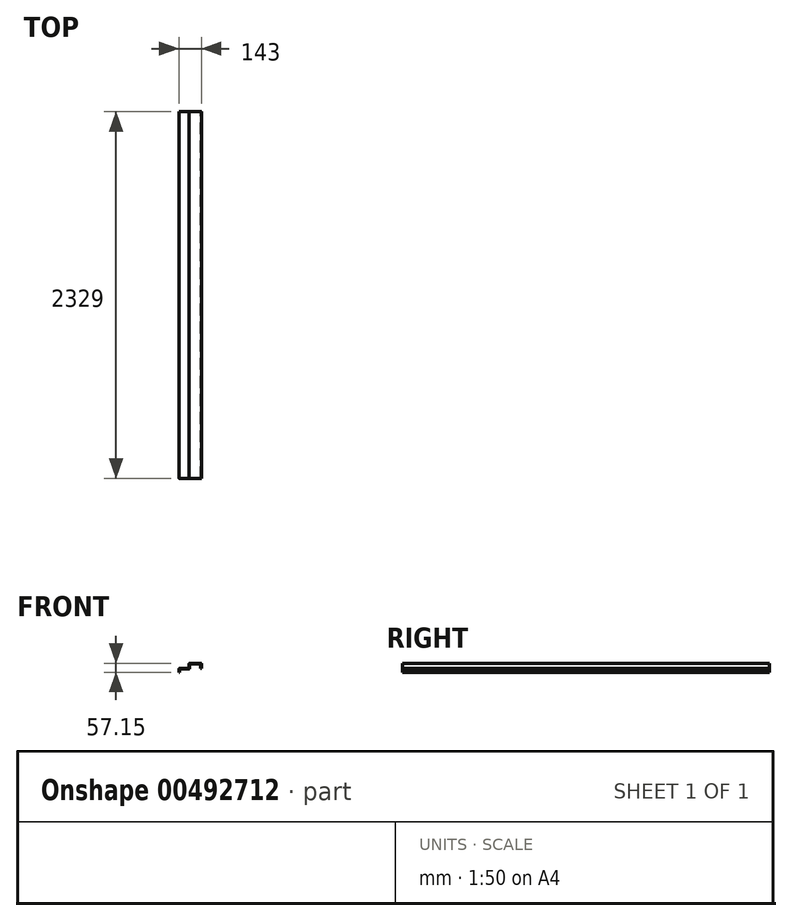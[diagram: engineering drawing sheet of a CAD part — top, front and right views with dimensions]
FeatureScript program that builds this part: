
annotation { "Feature Type Name" : "Feature", "Feature Type Description" : "" }
export const myFeature = defineFeature(function(context is Context, id is Id, definition is map)
    precondition{}
    {
        {
            var Q0;
            Q0=qCreatedBy(makeId("Front.planeOp"),FACE);
            var sketch = newSketch(context, id + "F0", { "sketchPlane" : qUnion([Q0])});
            skLineSegment(sketch, "E0", {"start": v(10, 0) * mm, "end": v(142, 0) * mm});
            skLineSegment(sketch, "E1", {"start": v(0, 10) * mm, "end": v(0, 120) * mm});
            skLineSegment(sketch, "E2", {"start": v(152, 10) * mm, "end": v(152, 147.25) * mm});
            skLineSegment(sketch, "E3.1", {"start": v(14.5, 4.5) * mm, "end": v(137.5, 4.5) * mm});
            skLineSegment(sketch, "E4", {"start": v(0, 120) * mm, "end": v(4.5, 120) * mm});
            skLineSegment(sketch, "E5", {"start": v(147.5, 147.25) * mm, "end": v(152, 147.25) * mm});
            skPoint(sketch, "E6.visualSharp", {"position": v(152, 0) * mm});
            skArc(sketch, "E6.filletArc", {"start": v(142, 0) * mm, "mid": v(149.07, 2.93) * mm, "end": v(152, 10) * mm});
            skPoint(sketch, "E7.visualSharp", {"position": v(147.5, 4.5) * mm});
            skArc(sketch, "E7.filletArc", {"start": v(137.5, 4.5) * mm, "mid": v(144.57, 7.43) * mm, "end": v(147.5, 14.5) * mm});
            skPoint(sketch, "E8.visualSharp", {"position": v(0, 0) * mm});
            skArc(sketch, "E8.filletArc", {"start": v(0, 10) * mm, "mid": v(2.93, 2.93) * mm, "end": v(10, 0) * mm});
            skPoint(sketch, "E9.visualSharp", {"position": v(4.5, 4.5) * mm});
            skArc(sketch, "E9.filletArc", {"start": v(4.5, 14.5) * mm, "mid": v(7.43, 7.43) * mm, "end": v(14.5, 4.5) * mm});
            skLineSegment(sketch, "E10", {"start": v(147.5, 146.75) * mm, "end": v(147.5, 120) * mm});
            skLineSegment(sketch, "E11", {"start": v(4.5, 94.6) * mm, "end": v(4.5, 115) * mm});
            skLineSegment(sketch, "E12", {"start": v(9.5, 120) * mm, "end": v(63, 120) * mm});
            skLineSegment(sketch, "E13", {"start": v(68, 125) * mm, "end": v(68, 146.75) * mm});
            skLineSegment(sketch, "E14", {"start": v(73, 151.75) * mm, "end": v(142.5, 151.75) * mm});
            skLineSegment(sketch, "E15.0", {"start": v(143, 142.25) * mm, "end": v(143, 120) * mm});
            skLineSegment(sketch, "E15.1", {"start": v(9, 94.6) * mm, "end": v(9, 110.5) * mm});
            skLineSegment(sketch, "E15.2", {"start": v(14, 115.5) * mm, "end": v(67.5, 115.5) * mm});
            skLineSegment(sketch, "E15.3", {"start": v(72.5, 120.5) * mm, "end": v(72.5, 142.25) * mm});
            skLineSegment(sketch, "E15.4", {"start": v(77.5, 147.25) * mm, "end": v(138, 147.25) * mm});
            skPoint(sketch, "E16.visualSharp", {"position": v(147.5, 151.75) * mm});
            skArc(sketch, "E16.filletArc", {"start": v(147.5, 146.75) * mm, "mid": v(146.04, 150.29) * mm, "end": v(142.5, 151.75) * mm});
            skPoint(sketch, "E17.visualSharp", {"position": v(143, 147.25) * mm});
            skArc(sketch, "E17.filletArc", {"start": v(143, 142.25) * mm, "mid": v(141.54, 145.79) * mm, "end": v(138, 147.25) * mm});
            skPoint(sketch, "E18.visualSharp", {"position": v(72.5, 147.25) * mm});
            skArc(sketch, "E18.filletArc", {"start": v(77.5, 147.25) * mm, "mid": v(73.96, 145.79) * mm, "end": v(72.5, 142.25) * mm});
            skPoint(sketch, "E19.visualSharp", {"position": v(68, 151.75) * mm});
            skArc(sketch, "E19.filletArc", {"start": v(73, 151.75) * mm, "mid": v(69.46, 150.29) * mm, "end": v(68, 146.75) * mm});
            skPoint(sketch, "E20.visualSharp", {"position": v(72.5, 115.5) * mm});
            skArc(sketch, "E20.filletArc", {"start": v(67.5, 115.5) * mm, "mid": v(71.04, 116.96) * mm, "end": v(72.5, 120.5) * mm});
            skPoint(sketch, "E21.visualSharp", {"position": v(68, 120) * mm});
            skArc(sketch, "E21.filletArc", {"start": v(63, 120) * mm, "mid": v(66.54, 121.46) * mm, "end": v(68, 125) * mm});
            skPoint(sketch, "E22.visualSharp", {"position": v(9, 115.5) * mm});
            skArc(sketch, "E22.filletArc", {"start": v(14, 115.5) * mm, "mid": v(10.46, 114.04) * mm, "end": v(9, 110.5) * mm});
            skPoint(sketch, "E23.visualSharp", {"position": v(4.5, 120) * mm});
            skArc(sketch, "E23.filletArc", {"start": v(9.5, 120) * mm, "mid": v(5.96, 118.54) * mm, "end": v(4.5, 115) * mm});
            skLineSegment(sketch, "E24", {"start": v(9, 94.6) * mm, "end": v(4.5, 94.6) * mm});
            skLineSegment(sketch, "E25", {"start": v(147.5, 120) * mm, "end": v(143, 120) * mm});
            skSolve(sketch);
        }
        {
            var Q0;
            Q0=makeQuery(id+"F0.imprint","IMPRINT",FACE,{"disambiguationData":[TD([[makeQuery(id+"F0.imprint","IMPRINT",EDGE,{"derivedFrom":sQuery(id+"F0.wireOp",EDGE,"E10")}),-1.0]])]});
            extrude(context, id + "F1", {"entities" : qUnion([Q0]), "depth" : 2329 * mm});
        }
    });
